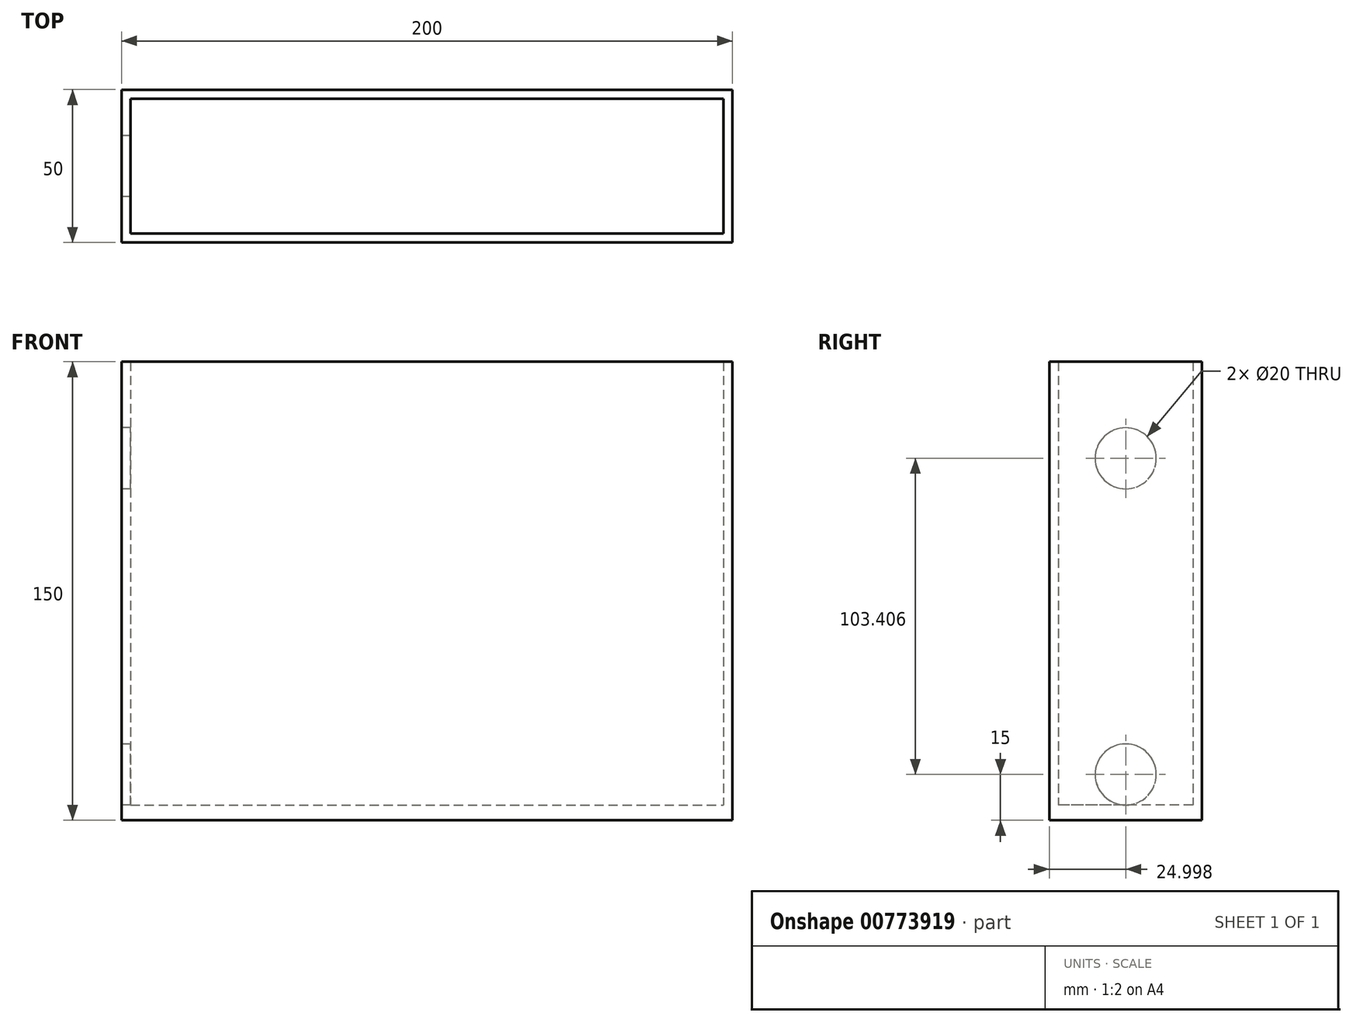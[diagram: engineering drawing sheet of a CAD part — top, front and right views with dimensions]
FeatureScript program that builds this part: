
annotation { "Feature Type Name" : "Feature", "Feature Type Description" : "" }
export const myFeature = defineFeature(function(context is Context, id is Id, definition is map)
    precondition{}
    {
        {
            var Q0;
            Q0=qCreatedBy(makeId("Top.planeOp"),FACE);
            var sketch = newSketch(context, id + "F0", { "sketchPlane" : qUnion([Q0])});
            skLineSegment(sketch, "E0.bottom", {"start": v(-98.15, 7.3) * mm, "end": v(101.85, 7.3) * mm});
            skLineSegment(sketch, "E0.top", {"start": v(-98.15, -42.7) * mm, "end": v(101.85, -42.7) * mm});
            skLineSegment(sketch, "E0.left", {"start": v(-98.15, 7.3) * mm, "end": v(-98.15, -42.7) * mm});
            skLineSegment(sketch, "E0.right", {"start": v(101.85, 7.3) * mm, "end": v(101.85, -42.7) * mm});
            skLineSegment(sketch, "E1.bottom", {"start": v(-95.15, 4.3) * mm, "end": v(98.85, 4.3) * mm});
            skLineSegment(sketch, "E1.top", {"start": v(-95.15, -39.7) * mm, "end": v(98.85, -39.7) * mm});
            skLineSegment(sketch, "E1.left", {"start": v(-95.15, 4.3) * mm, "end": v(-95.15, -39.7) * mm});
            skLineSegment(sketch, "E1.right", {"start": v(98.85, 4.3) * mm, "end": v(98.85, -39.7) * mm});
            skSolve(sketch);
        }
        {
            var Q0;
            Q0=makeQuery(id+"F0.imprint","IMPRINT",FACE,{"disambiguationData":[TD([[makeQuery(id+"F0.imprint","IMPRINT",EDGE,{"derivedFrom":sQuery(id+"F0.wireOp",EDGE,"E0.bottom")}),-1.0]])]});
            extrude(context, id + "F1", {"entities" : qUnion([Q0]), "depth" : 150 * mm, "offsetDistance" : 25.4 * mm});
        }
        {
            var Q0;
            Q0=makeQuery(id+"F0.imprint","IMPRINT",FACE,{"disambiguationData":[TD([[makeQuery(id+"F0.imprint","IMPRINT",EDGE,{"derivedFrom":sQuery(id+"F0.wireOp",EDGE,"E1.bottom")}),-1.0]])]});
            extrude(context, id + "F2", {"entities" : qUnion([Q0]), "operationType" : NewBodyOperationType.ADD, "depth" : 5 * mm, "offsetDistance" : 25.4 * mm});
        }
        {
            var Q0;
            Q0=makeQuery(id+"F1.opExtrude","SWEPT_FACE",FACE,{"disambiguationData":[OSD([sQuery(id+"F0.wireOp",EDGE,"E0.left")])]});
            var sketch = newSketch(context, id + "F3", { "sketchPlane" : qUnion([Q0])});
            skCircle(sketch, "E2", {"center": v(17.7, 118.4) * mm, "radius": 10 * mm});
            skCircle(sketch, "E3", {"center": v(17.7, 15) * mm, "radius": 10 * mm});
            skSolve(sketch);
        }
        {
            var Q0;
            Q0=makeQuery(id+"F3.imprint","IMPRINT",FACE,{"disambiguationData":[TD([[makeQuery(id+"F3.imprint","IMPRINT",EDGE,{"derivedFrom":sQuery(id+"F3.wireOp",EDGE,"E2")}),1.0]])]});
            var Q1;
            Q1=sQuery(id+"F3.wireOp",EDGE,"E2");
            extrude(context, id + "F4", {"entities" : qUnion([Q0]), "operationType" : NewBodyOperationType.REMOVE, "surfaceEntities" : qUnion([Q1]), "oppositeDirection" : true, "depth" : 25.4 * mm, "offsetDistance" : 25.4 * mm});
        }
        {
            var Q0;
            Q0=makeQuery(id+"F3.imprint","IMPRINT",FACE,{"disambiguationData":[TD([[makeQuery(id+"F3.imprint","IMPRINT",EDGE,{"derivedFrom":sQuery(id+"F3.wireOp",EDGE,"E3")}),1.0]])]});
            var Q1;
            Q1=sQuery(id+"F3.wireOp",EDGE,"E3");
            extrude(context, id + "F5", {"entities" : qUnion([Q0]), "operationType" : NewBodyOperationType.REMOVE, "surfaceEntities" : qUnion([Q1]), "oppositeDirection" : true, "depth" : 25.4 * mm, "offsetDistance" : 25.4 * mm});
        }
    });
